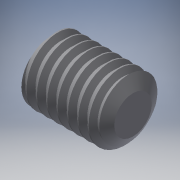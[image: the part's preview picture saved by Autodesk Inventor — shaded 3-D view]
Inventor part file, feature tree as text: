
AUTODESK INVENTOR PART (.ipt)
format: ipt  version: 2019 (Build 230136000, 136)  size: 696,832 bytes
history: native  units: in
note: dims shown in document units (in); Inventor stores cm internally (conversion verified against a paired STEP export)
features: extrude x1, sketch x1, other x1
ambient origin geometry x8: Origin, YZ Plane, XZ Plane, XY Plane, X Axis, Y Axis, Z Axis, Center Point
bodies: Solid1 (feature_tree)
feature tree (3):
  extrude  "Extrusion1"  [1 undecoded]
  sketch  "Sketch1"  dims[d0=3.937in d1=0.0in]
  other  "PartBody"
note: 1 required parameter value undecoded (feature->parameter linkage not recoverable at this tier; creation-order binding heuristic only, values carry confidence <= 0.55)
